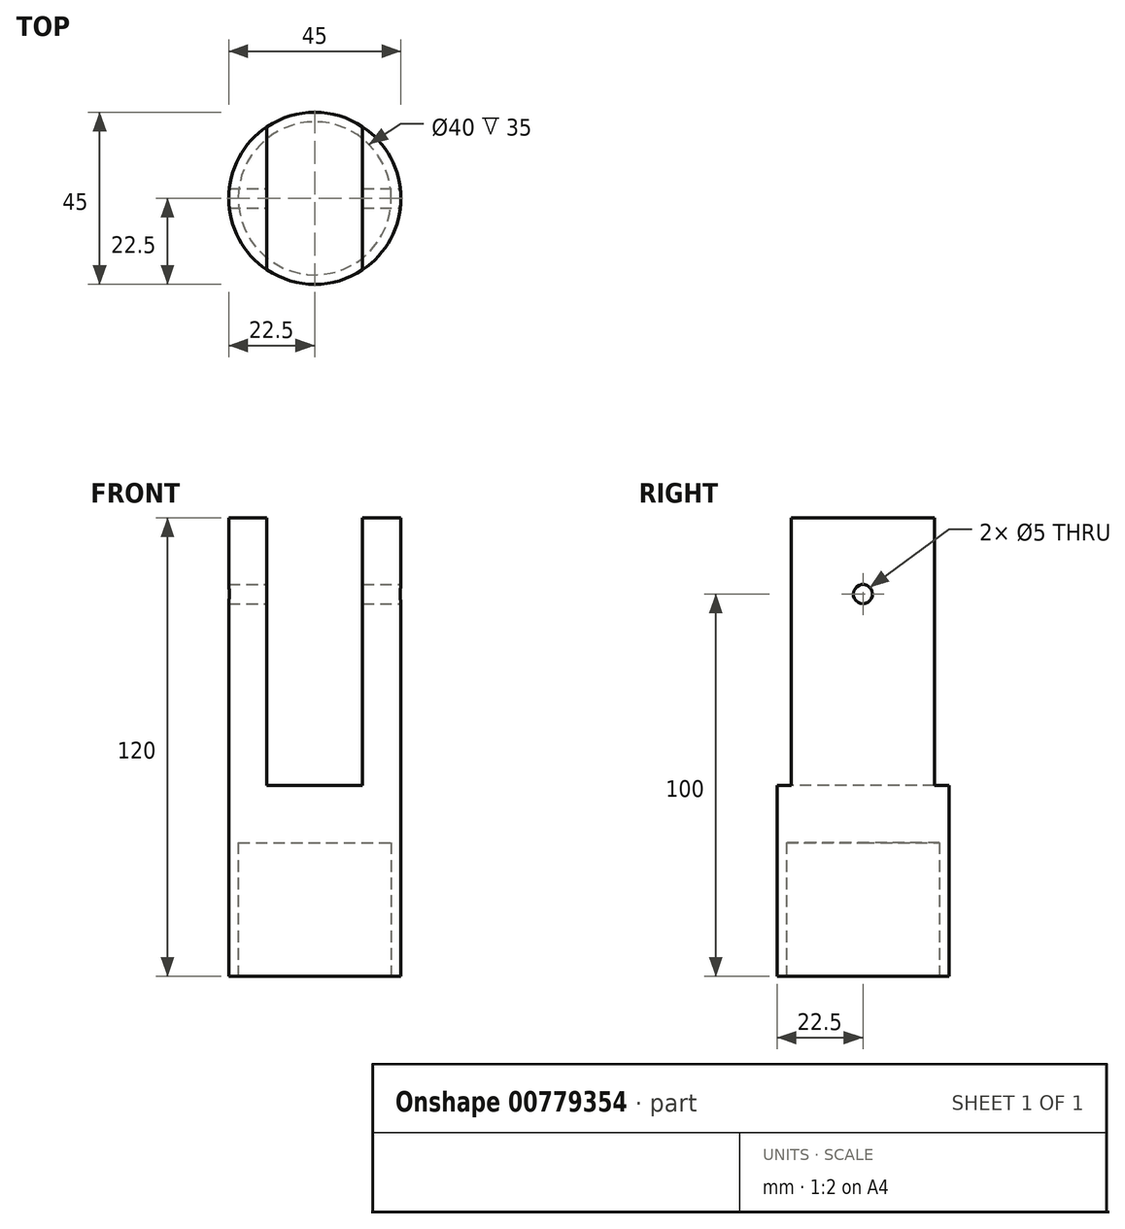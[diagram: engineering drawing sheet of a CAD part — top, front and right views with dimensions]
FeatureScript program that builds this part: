
annotation { "Feature Type Name" : "Feature", "Feature Type Description" : "" }
export const myFeature = defineFeature(function(context is Context, id is Id, definition is map)
    precondition{}
    {
        {
            var Q0;
            Q0=qCreatedBy(makeId("Top.planeOp"),FACE);
            var sketch = newSketch(context, id + "F0", { "sketchPlane" : qUnion([Q0])});
            skCircle(sketch, "E0", {"center": v(0, 0) * mm, "radius": 22.5 * mm});
            skSolve(sketch);
        }
        {
            var Q0;
            Q0=makeQuery(id+"F0.imprint","IMPRINT",FACE,{"disambiguationData":[TD([[makeQuery(id+"F0.imprint","IMPRINT",EDGE,{"derivedFrom":sQuery(id+"F0.wireOp",EDGE,"E0")}),1.0]])]});
            var Q1;
            Q1 = qSketchRegion(id + "F2", true);
            extrude(context, id + "F1", {"entities" : qUnion([Q0, Q1]), "flatOperationType" : FlatOperationType.REMOVE, "depth" : 120 * mm, "offsetDistance" : 25 * mm, "domain" : OperationDomain.MODEL});
        }
        {
            var Q0;
            Q0=makeQuery(id+"F1.opExtrude","CAP_FACE",FACE,{"disambiguationData":[OSD([sQuery(id+"F0.wireOp",EDGE,"E0")])],"isStart":false});
            var sketch = newSketch(context, id + "F2", { "sketchPlane" : qUnion([Q0])});
            skLineSegment(sketch, "E1", {"start": v(-12.5, 18.7) * mm, "end": v(-12.5, -18.7) * mm});
            skLineSegment(sketch, "E2", {"start": v(12.5, 18.7) * mm, "end": v(12.5, -18.7) * mm});
            skSolve(sketch);
        }
        {
            var Q0;
            {var subQ0=sQuery(id+"F2.wireOp",EDGE,"E1");Q0=makeQuery(id+"F2.imprint","IMPRINT",FACE,{"disambiguationData":[TD([[makeQuery(id+"F2.imprint","IMPRINT",EDGE,{"derivedFrom":subQ0}),1.0]])]});}
            extrude(context, id + "F3", {"entities" : qUnion([Q0]), "operationType" : NewBodyOperationType.REMOVE, "flatOperationType" : FlatOperationType.REMOVE, "oppositeDirection" : true, "depth" : 70 * mm, "offsetDistance" : 25 * mm, "domain" : OperationDomain.MODEL});
        }
        {
            var Q0;
            Q0=makeQuery(id+"F1.opExtrude","CAP_FACE",FACE,{"disambiguationData":[OSD([sQuery(id+"F0.wireOp",EDGE,"E0")])],"isStart":true});
            var sketch = newSketch(context, id + "F4", { "sketchPlane" : qUnion([Q0])});
            skCircle(sketch, "E3", {"center": v(0, 0) * mm, "radius": 20 * mm});
            skSolve(sketch);
        }
        {
            var Q0;
            Q0=makeQuery(id+"F4.imprint","IMPRINT",FACE,{"disambiguationData":[TD([[makeQuery(id+"F4.imprint","IMPRINT",EDGE,{"derivedFrom":sQuery(id+"F4.wireOp",EDGE,"E3")}),1.0]])]});
            extrude(context, id + "F5", {"entities" : qUnion([Q0]), "operationType" : NewBodyOperationType.REMOVE, "flatOperationType" : FlatOperationType.REMOVE, "oppositeDirection" : true, "depth" : 35 * mm, "offsetDistance" : 25 * mm, "domain" : OperationDomain.MODEL});
        }
        {
            var Q0;
            Q0=qCreatedBy(makeId("Right.planeOp"),FACE);
            cPlane(context, id + "F6", {"entities" : qUnion([Q0]), "cplaneType" : CPlaneType.OFFSET, "offset" : 22.5 * mm, "width" : 150 * mm, "height" : 150 * mm});
        }
        {
            var Q0;
            Q0=qCreatedBy(id+"F6.planeOp",FACE);
            var sketch = newSketch(context, id + "F7", { "sketchPlane" : qUnion([Q0])});
            skLineSegment(sketch, "E4", {"start": v(-18.7, 100) * mm, "end": v(18.7, 100) * mm});
            skPoint(sketch, "E5", {"position": v(0, 100) * mm});
            skSolve(sketch);
        }
        {
            var Q0;
            Q0=sQuery(id+"F7.wireOp",VERTEX,"E5");
            var Q1;
            Q1=makeQuery(id+"F1.opExtrude","SWEPT_BODY",BODY,{"disambiguationData":[OSD([sQuery(id+"F0.wireOp",EDGE,"E0")])]});
            hole(context, id + "F8", {"style" : HoleStyle.SIMPLE, "endStyle" : HoleEndStyle.THROUGH, "holeDiameter" : 5 * mm, "majorDiameter" : 5 * mm, "isTappedThrough" : true, "tappedDepth" : 12 * mm, "tapClearance" : 3, "locations" : qUnion([Q0]), "scope" : qUnion([Q1])});
        }
    });
